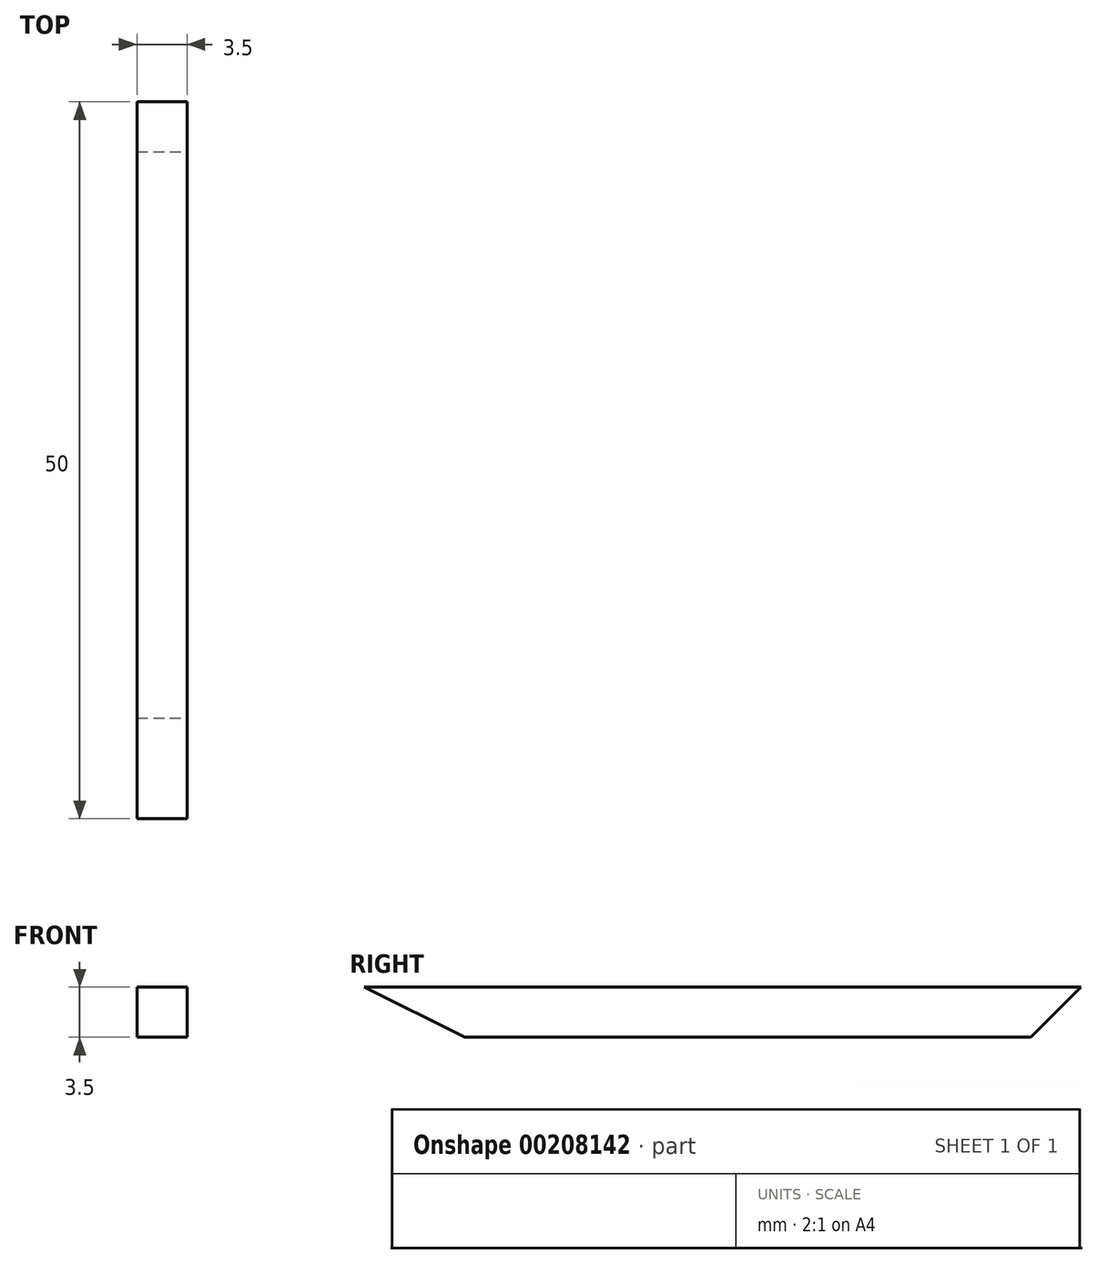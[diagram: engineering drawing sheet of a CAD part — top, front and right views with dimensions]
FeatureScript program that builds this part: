
annotation { "Feature Type Name" : "Feature", "Feature Type Description" : "" }
export const myFeature = defineFeature(function(context is Context, id is Id, definition is map)
    precondition{}
    {
        {
            var Q0;
            Q0=qCreatedBy(makeId("Top.planeOp"),FACE);
            var sketch = newSketch(context, id + "F0", { "sketchPlane" : qUnion([Q0])});
            skLineSegment(sketch, "E0.bottom", {"start": v(1.75, -25) * mm, "end": v(-1.75, -25) * mm});
            skLineSegment(sketch, "E0.top", {"start": v(1.75, 25) * mm, "end": v(-1.75, 25) * mm});
            skLineSegment(sketch, "E0.left", {"start": v(1.75, -25) * mm, "end": v(1.75, 25) * mm});
            skLineSegment(sketch, "E0.right", {"start": v(-1.75, -25) * mm, "end": v(-1.75, 25) * mm});
            skPoint(sketch, "E0.middle", {"position": v(0, 0) * mm});
            skSolve(sketch);
        }
        {
            var Q0;
            Q0 = qSketchRegion(id + "F0", true);
            extrude(context, id + "F1", {"entities" : qUnion([Q0]), "depth" : 3.5 * mm});
        }
        {
            var Q0;
            Q0=makeQuery(id+"F1.opExtrude","SWEPT_FACE",FACE,{"disambiguationData":[OSD([sQuery(id+"F0.wireOp",EDGE,"E0.left")])]});
            var sketch = newSketch(context, id + "F2", { "sketchPlane" : qUnion([Q0])});
            skLineSegment(sketch, "E1", {"start": v(-25, 3.5) * mm, "end": v(-18, 0) * mm});
            skLineSegment(sketch, "E2", {"start": v(-18, 0) * mm, "end": v(-25, 0) * mm});
            skLineSegment(sketch, "E3", {"start": v(-25, 0) * mm, "end": v(-25, 3.5) * mm});
            skLineSegment(sketch, "E4", {"start": v(25, 3.5) * mm, "end": v(21.5, 0) * mm});
            skLineSegment(sketch, "E5", {"start": v(21.5, 0) * mm, "end": v(25, 0) * mm});
            skLineSegment(sketch, "E6", {"start": v(25, 0) * mm, "end": v(25, 3.5) * mm});
            skSolve(sketch);
        }
        {
            var Q0;
            Q0 = qSketchRegion(id + "F2", true);
            extrude(context, id + "F3", {"entities" : qUnion([Q0]), "operationType" : NewBodyOperationType.REMOVE, "endBound" : BoundingType.THROUGH_ALL, "oppositeDirection" : true, "depth" : 25.4 * mm});
        }
    });
